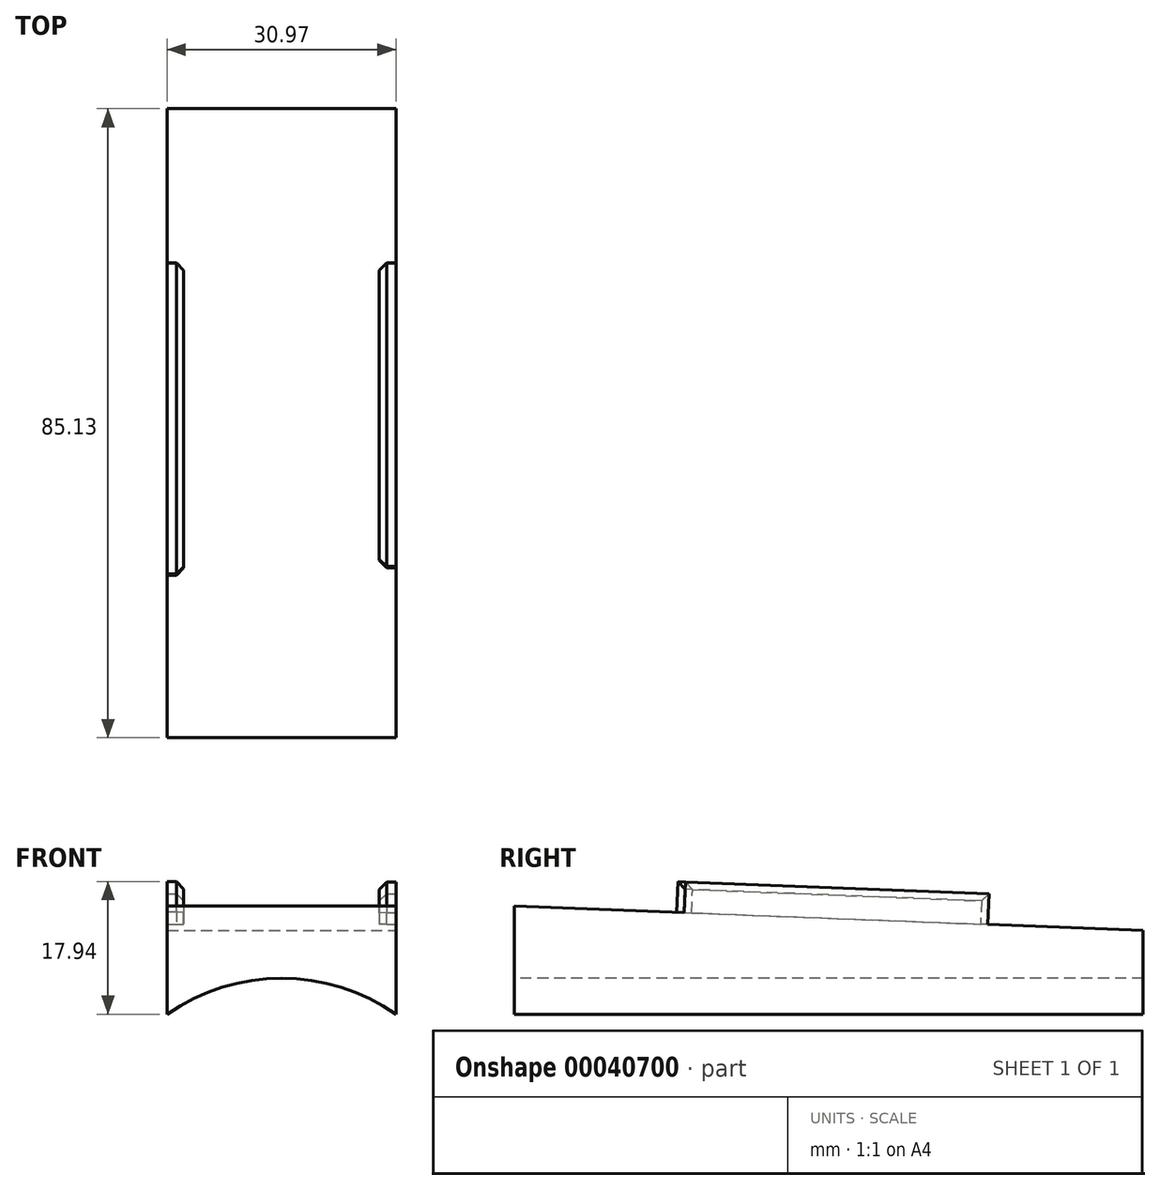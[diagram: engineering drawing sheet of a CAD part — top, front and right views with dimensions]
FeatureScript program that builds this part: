
annotation { "Feature Type Name" : "Feature", "Feature Type Description" : "" }
export const myFeature = defineFeature(function(context is Context, id is Id, definition is map)
    precondition{}
    {
        {
            var Q0;
            Q0=qCreatedBy(makeId("Right.planeOp"),FACE);
            var sketch = newSketch(context, id + "F0", { "sketchPlane" : qUnion([Q0])});
            skLineSegment(sketch, "E0.left", {"start": v(97.66, 34.64) * mm, "end": v(97.66, 28.3) * mm});
            skLineSegment(sketch, "E1", {"start": v(97.66, 28.3) * mm, "end": v(12.53, 28.3) * mm});
            skLineSegment(sketch, "E2", {"start": v(12.53, 28.3) * mm, "end": v(12.53, 37.95) * mm});
            skLineSegment(sketch, "E3", {"start": v(12.53, 37.95) * mm, "end": v(97.66, 34.64) * mm});
            skSolve(sketch);
        }
        {
            var Q0;
            Q0 = qSketchRegion(id + "F0", true);
            extrude(context, id + "F1", {"entities" : qUnion([Q0]), "oppositeDirection" : true, "depth" : 30.97 * mm});
        }
        {
            var Q0;
            Q0=makeQuery(id+"F1.opExtrude","SWEPT_FACE",FACE,{"disambiguationData":[OSD([sQuery(id+"F0.wireOp",EDGE,"E3")])]});
            var sketch = newSketch(context, id + "F2", { "sketchPlane" : qUnion([Q0])});
            skLineSegment(sketch, "E4.left", {"start": v(0, 34.08) * mm, "end": v(0, 75.21) * mm});
            skLineSegment(sketch, "E4.right", {"start": v(-2.25, 34.08) * mm, "end": v(-2.25, 75.21) * mm});
            skLineSegment(sketch, "E5.left", {"start": v(-30.97, 33.04) * mm, "end": v(-30.97, 75.21) * mm});
            skLineSegment(sketch, "E5.right", {"start": v(-28.72, 33.04) * mm, "end": v(-28.72, 75.21) * mm});
            skLineSegment(sketch, "E6", {"start": v(-28.72, 33.04) * mm, "end": v(-30.97, 33.04) * mm});
            skLineSegment(sketch, "E7", {"start": v(-2.25, 34.08) * mm, "end": v(0, 34.08) * mm});
            skLineSegment(sketch, "E8", {"start": v(-30.97, 75.21) * mm, "end": v(-28.72, 75.21) * mm});
            skLineSegment(sketch, "E9", {"start": v(-2.25, 75.21) * mm, "end": v(0, 75.21) * mm});
            skPoint(sketch, "E5.top.start.orphan", {"position": v(-30.97, 97.21) * mm});
            skPoint(sketch, "E5.bottom.start.orphan", {"position": v(-30.97, 11.04) * mm});
            skSolve(sketch);
        }
        {
            var Q0;
            Q0 = qSketchRegion(id + "F2", true);
            extrude(context, id + "F3", {"entities" : qUnion([Q0]), "operationType" : NewBodyOperationType.ADD, "depth" : 4.15 * mm});
        }
        {
            var Q0;
            Q0=makeQuery(id+"F3.opExtrude","CAP_EDGE",EDGE,{"disambiguationData":[OSD([sQuery(id+"F2.wireOp",EDGE,"E5.right")])],"isStart":false});
            var Q1;
            Q1=makeQuery(id+"F3.opExtrude","CAP_EDGE",EDGE,{"disambiguationData":[OSD([sQuery(id+"F2.wireOp",EDGE,"E4.right")])],"isStart":false});
            chamfer(context, id + "F4", {"entities" : qUnion([Q0, Q1]), "width" : 1 * mm, "tangentPropagation" : true});
        }
        {
            var Q0;
            Q0=makeQuery(id+"F3.opExtrude","SWEPT_EDGE",EDGE,{"disambiguationData":[OSD([sQuery(id+"F0.wireOp",EDGE,"E2"),sQuery(id+"F0.wireOp",EDGE,"E3"),sQuery(id+"F2.wireOp",EDGE,"E5.bottom"),sQuery(id+"F2.wireOp",EDGE,"E5.right")])]});
            var Q1;
            Q1=makeQuery(id+"F3.opExtrude","SWEPT_EDGE",EDGE,{"disambiguationData":[OSD([sQuery(id+"F0.wireOp",EDGE,"E2"),sQuery(id+"F0.wireOp",EDGE,"E3"),sQuery(id+"F2.wireOp",EDGE,"E4.bottom"),sQuery(id+"F2.wireOp",EDGE,"E4.right")])]});
            chamfer(context, id + "F5", {"entities" : qUnion([Q0, Q1]), "width" : 1 * mm, "tangentPropagation" : true});
        }
        {
            var Q0;
            Q0=makeQuery(id+"F1.opExtrude","SWEPT_FACE",FACE,{"disambiguationData":[OSD([sQuery(id+"F0.wireOp",EDGE,"E2")])]});
            var sketch = newSketch(context, id + "F6", { "sketchPlane" : qUnion([Q0])});
            skLineSegment(sketch, "E10", {"start": v(-30.97, 28.3) * mm, "end": v(-30.97, 23.3) * mm});
            skLineSegment(sketch, "E11", {"start": v(0, 23.3) * mm, "end": v(0, 28.3) * mm});
            skArc(sketch, "E12", {"start": v(0, 23.3) * mm, "mid": v(-15.49, 28.17) * mm, "end": v(-30.97, 23.3) * mm});
            skLineSegment(sketch, "E13", {"start": v(-30.97, 28.3) * mm, "end": v(0, 28.3) * mm});
            skSolve(sketch);
        }
        {
            var Q0;
            Q0 = qSketchRegion(id + "F6", true);
            var Q1;
            Q1=makeQuery(id+"F1.opExtrude","SWEPT_FACE",FACE,{"disambiguationData":[OSD([sQuery(id+"F0.wireOp",EDGE,"E0.left")])]});
            extrude(context, id + "F7", {"entities" : qUnion([Q0]), "operationType" : NewBodyOperationType.ADD, "endBound" : BoundingType.UP_TO_SURFACE, "oppositeDirection" : true, "endBoundEntityFace" : qUnion([Q1]), "depth" : 25 * mm});
        }
    });
